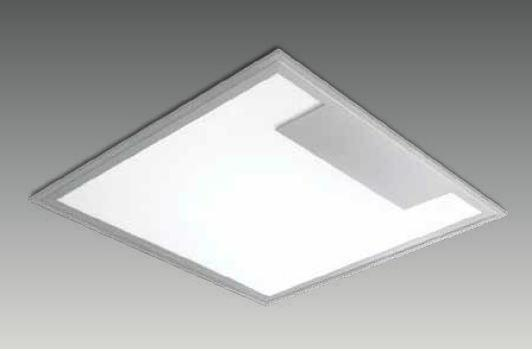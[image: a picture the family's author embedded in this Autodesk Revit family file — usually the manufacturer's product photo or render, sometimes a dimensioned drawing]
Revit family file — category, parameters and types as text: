
# Revit family: G 6060 MIR
name_source: partatom
category: Lighting Fixtures
revit_build: Autodesk Revit 2017 (Build: 20160225_1515(x64)
units: mm (PartAtom-declared; Revit-internal decimal feet)

## family parameters
Always vertical = Yes
Cut with Voids When Loaded = No
Host = Ceiling
Light Source = Yes
OmniClass Number = 23.80.70.11
OmniClass Title = Luminaries for Internal Lighting
Part Type = Normal
Room Calculation Point = No
Round Connector Dimension = Use Diameter
Shared = No

## types (4) — shared parameters
Color Filter = 16777215
Dimming Lamp Color Temperature Shift = <None>
Emit Shape Visible in Rendering = Yes
Emit from Rectangle Length = 570 mm  [stored 1.87008 ft]
Emit from Rectangle Width = 570 mm  [stored 1.87008 ft]
Light Source Symbol Size = 610 mm
Manufacturer = ARLIGHT
Type Image = G 6060 MIR.JPG

## per-type parameters (varying)
| type | Wattage Comments |
| GMIR.6060.36.30 | 36 |
| GMIR.6060.36.40 | 36 |
| GMIR.6060.28.30 | 28 |
| GMIR.6060.28.40 | 28 |

note: [stored X ft] marks values corroborated as IEEE doubles in the binary element streams (Revit-internal decimal feet)

## geometry (parser evidence)
native form markers: Sweep x2
no freeform markers — native parametric forms only
